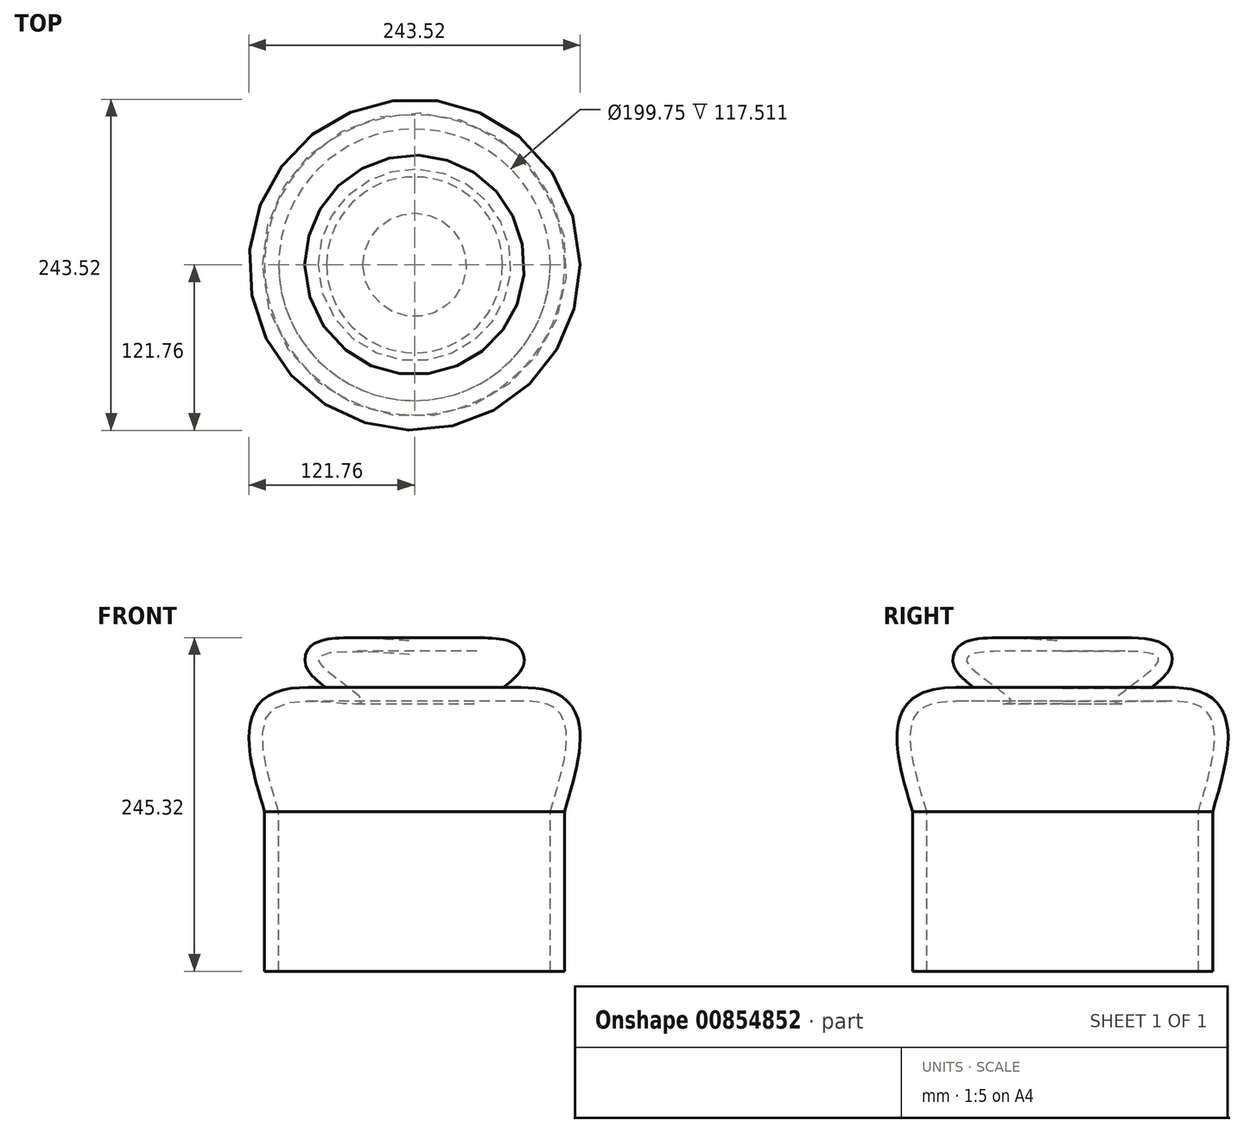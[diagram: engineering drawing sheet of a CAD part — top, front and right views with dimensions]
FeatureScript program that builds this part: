
annotation { "Feature Type Name" : "Feature", "Feature Type Description" : "" }
export const myFeature = defineFeature(function(context is Context, id is Id, definition is map)
    precondition{}
    {
        {
            var Q0;
            Q0=qCreatedBy(makeId("Front.planeOp"),FACE);
            var sketch = newSketch(context, id + "F0", { "sketchPlane" : qUnion([Q0])});
            skLineSegment(sketch, "E0", {"start": v(0, 169.58) * mm, "end": v(0, -108.02) * mm, "construction": true});
            skLineSegment(sketch, "E1", {"start": v(0, 0) * mm, "end": v(-99.87, 0) * mm});
            skFitSpline(sketch, "E2", {"points": [v(-99.87, 0) * mm, v(-99.87, 77.85) * mm, v(-38.02, 80.87) * mm, v(-70.3, 110.13) * mm, v(0, 115.57) * mm], "startDerivative": vector(-110.89, 367.98) * mm, "endDerivative": vector(423.03, -28.8) * mm});
            skLineSegment(sketch, "E3", {"start": v(0, 115.57) * mm, "end": v(0, 0) * mm});
            skSolve(sketch);
        }
        {
            var Q0;
            Q0 = qSketchRegion(id + "F0", true);
            var Q1;
            Q1=sQuery(id+"F0.wireOp",EDGE,"E3");
            revolve(context, id + "F1", {"surfaceOperationType" : NewSurfaceOperationType.NEW, "entities" : qUnion([Q0]), "axis" : qUnion([Q1]), "revolveType" : RevolveType.FULL});
        }
        {
            var Q0;
            Q0=makeQuery(id+"F1.opRevolve","SWEPT_FACE",FACE,{"disambiguationData":[OSD([sQuery(id+"F0.wireOp",EDGE,"E1")])]});
            shell(context, id + "F2", {"entities" : qUnion([Q0]), "thickness" : 10 * mm, "oppositeDirection" : true});
        }
        {
            var Q0;
            Q0=makeQuery(id+"F1.opRevolve","SWEPT_FACE",FACE,{"disambiguationData":[OSD([sQuery(id+"F0.wireOp",EDGE,"E1")])]});
            extrude(context, id + "F3", {"entities" : qUnion([Q0]), "operationType" : NewBodyOperationType.ADD, "depth" : 117.51 * mm, "offsetDistance" : 25.4 * mm});
        }
    });
